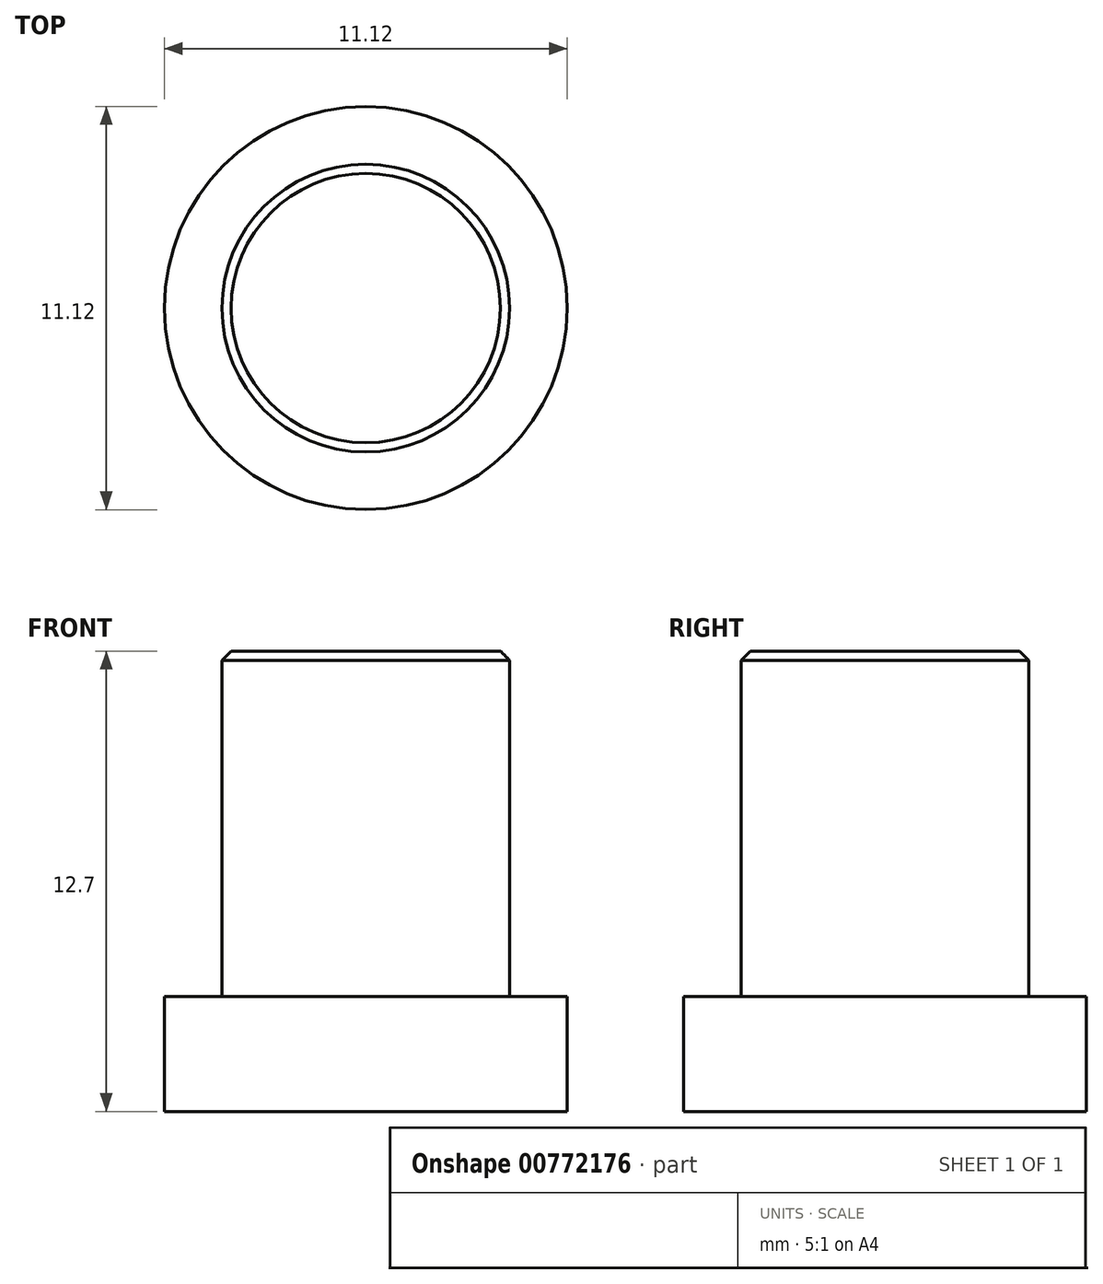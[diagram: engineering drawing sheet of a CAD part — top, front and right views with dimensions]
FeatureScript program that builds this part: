
annotation { "Feature Type Name" : "Feature", "Feature Type Description" : "" }
export const myFeature = defineFeature(function(context is Context, id is Id, definition is map)
    precondition{}
    {
        {
            var Q0;
            Q0=qCreatedBy(makeId("Top.planeOp"),FACE);
            var sketch = newSketch(context, id + "F0", { "sketchPlane" : qUnion([Q0])});
            skCircle(sketch, "E0", {"center": v(0, 0) * mm, "radius": 5.56 * mm});
            skSolve(sketch);
        }
        {
            var Q0;
            Q0 = qSketchRegion(id + "F0", true);
            extrude(context, id + "F1", {"entities" : qUnion([Q0]), "depth" : 3.17 * mm, "offsetDistance" : 25.4 * mm});
        }
        {
            var Q0;
            Q0=makeQuery(id+"F1.opExtrude","CAP_FACE",FACE,{"disambiguationData":[OSD([sQuery(id+"F0.wireOp",EDGE,"E0")])],"isStart":false});
            var sketch = newSketch(context, id + "F2", { "sketchPlane" : qUnion([Q0])});
            skCircle(sketch, "E1.0.0", {"center": v(0, 0) * mm, "radius": 5.56 * mm});
            skCircle(sketch, "E2", {"center": v(0, 0) * mm, "radius": 3.97 * mm});
            skSolve(sketch);
        }
        {
            var Q0;
            Q0=makeQuery(id+"F2.imprint","IMPRINT",FACE,{"disambiguationData":[TD([[makeQuery(id+"F2.imprint","IMPRINT",EDGE,{"derivedFrom":sQuery(id+"F2.wireOp",EDGE,"E2")}),1.0]])]});
            extrude(context, id + "F3", {"entities" : qUnion([Q0]), "operationType" : NewBodyOperationType.ADD, "depth" : 9.52 * mm, "offsetDistance" : 25.4 * mm});
        }
        {
            var Q0;
            Q0=makeQuery(id+"F3.opExtrude","CAP_EDGE",EDGE,{"disambiguationData":[OSD([sQuery(id+"F2.wireOp",EDGE,"E2")])],"isStart":false});
            chamfer(context, id + "F4", {"entities" : qUnion([Q0]), "width" : 0.25 * mm, "tangentPropagation" : true});
        }
    });
